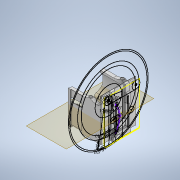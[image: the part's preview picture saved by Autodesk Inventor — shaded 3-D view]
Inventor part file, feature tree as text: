
AUTODESK INVENTOR PART (.ipt)
format: ipt  version: 2022 (Build 260153000, 153)  size: 979,968 bytes
history: native  units: mm
features: sketch x25, reference x24, extrude x23, projected_geometry x19, fillet x15, other x12, chamfer x2
ambient origin geometry x8: Origin, YZ Plane, XZ Plane, XY Plane, X Axis, Y Axis, Z Axis, Center Point
bodies: Body1 (feature_tree)
feature tree (120):
  other  "Твердое тело1"
  extrude  "Выдавливание1"  Depth=34.5mm TaperAngle=0.0deg
  extrude  "Выдавливание2"  Depth=0.5mm
  extrude  "Выдавливание3"  Depth=0.3mm
  extrude  "Выдавливание4"  Depth=5.0mm
  extrude  "Выдавливание5"  Depth=5.0mm
  extrude  "Выдавливание6"  Depth=5.0mm
  extrude  "Выдавливание8"  Depth=15.0mm
  extrude  "Выдавливание9"  Depth=15.0mm
  chamfer  "Фаска1"  Distance=15.0mm
  fillet  "Сопряжение1"  Radius=1.7mm
  extrude  "Выдавливание10"  Depth=2.0mm TaperAngle=0.0deg
  extrude  "Выдавливание11"  Depth=0.8mm
  fillet  "Сопряжение2"  Radius=4.7mm
  fillet  "Сопряжение3"  Radius=0.4mm
  fillet  "Сопряжение4"  Radius=0.4mm
  fillet  "Сопряжение5"  Radius=200.0mm
  sketch  "Эскиз15"
  extrude  "Выдавливание12"  Depth=0.5mm TaperAngle=0.0deg
  sketch  "Эскиз17"
  extrude  "Выдавливание13"  Depth=2.3mm TaperAngle=0.0deg
  extrude  "Выдавливание18"  Depth=10.0mm
  extrude  "Выдавливание19"  Depth=10.0mm
  extrude  "Выдавливание20"  Depth=3.0mm
  chamfer  "Фаска2"  Distance=4.0mm
  other  "РабПлоскость1"
  extrude  "Выдавливание21"  Depth=3.0mm
  fillet  "Сопряжение16"  Radius=4.0mm
  fillet  "Сопряжение17"  Radius=2.3mm
  fillet  "Сопряжение18"  Radius=2.3mm
  extrude  "Выдавливание22"  Depth=10.0mm
  fillet  "Сопряжение19"  Radius=45.0mm
  extrude  "Выдавливание23"  Depth=30.0mm
  extrude  "Выдавливание24"  Depth=0.8mm TaperAngle=0.0deg
  fillet  "Сопряжение20"  Radius=2.0mm
  extrude  "Выдавливание25"  Depth=1.5mm
  fillet  "Сопряжение21"  Radius=0.15mm
  extrude  "Выдавливание26"  Depth=3.0mm
  fillet  "Сопряжение22"  Radius=50.0mm
  fillet  "Сопряжение23"  Radius=4.0mm
  fillet  "Сопряжение24"  Radius=4.0mm
  extrude  "Выдавливание27"  Depth=3.2mm
  extrude  "Выдавливание28"  Depth=8.0mm
  fillet  "Сопряжение25"  Radius=2.2mm
  sketch  "Эскиз1"
  reference  "Ссылка1"
  reference  "Ссылка2"
  reference  "Ссылка3"
  reference  "Ссылка4"
  reference  "Ссылка5"
  reference  "Ссылка6"
  reference  "Ссылка7"
  reference  "Ссылка8"
  sketch  "Эскиз2"
  projected_geometry  "Спроецированная петля1"
  projected_geometry  "Спроецированная петля2"
  sketch  "Эскиз3"
  reference  "Ссылка9"
  reference  "Ссылка10"
  sketch  "Эскиз4"
  projected_geometry  "Спроецированная петля3"
  reference  "Ссылка11"
  reference  "Ссылка12"
  reference  "Ссылка13"
  reference  "Ссылка14"
  sketch  "Эскиз5"
  reference  "Ссылка15"
  reference  "Ссылка16"
  projected_geometry  "Спроецированная петля4"
  sketch  "Эскиз7"
  projected_geometry  "Спроецированная петля6"
  sketch  "Эскиз11"
  projected_geometry  "Спроецированная петля8"
  sketch  "Эскиз12"
  reference  "Ссылка27"
  sketch  "Эскиз13"
  reference  "Ссылка28"
  projected_geometry  "Спроецированная петля9"
  sketch  "Эскиз14"
  sketch  "Эскиз16"
  reference  "Ссылка29"
  projected_geometry  "Спроецированная петля10"
  projected_geometry  "Спроецированная петля11"
  projected_geometry  "Спроецированная петля12"
  reference  "Ссылка30"
  reference  "Ссылка31"
  sketch  "Эскиз18"
  projected_geometry  "Спроецированная петля14"
  sketch  "Эскиз23"
  sketch  "Эскиз24"
  projected_geometry  "Спроецированная петля24"
  sketch  "Эскиз25"
  sketch  "Эскиз26"
  sketch  "Эскиз27"
  projected_geometry  "Спроецированная петля25"
  sketch  "Эскиз28"
  sketch  "Эскиз29"
  projected_geometry  "Спроецированная петля26"
  sketch  "Эскиз30"
  projected_geometry  "Спроецированная петля27"
  projected_geometry  "Спроецированная петля28"
  projected_geometry  "Спроецированная петля29"
  reference  "Ссылка32"
  reference  "Ссылка33"
  sketch  "Эскиз31"
  reference  "Ссылка34"
  sketch  "Эскиз32"
  sketch  "Эскиз33"
  projected_geometry  "Спроецированная петля30"
  projected_geometry  "Спроецированная петля31"
  other  "<userpath>\OneDrive\Документы\Git\MZCAT_battery\FastBattery.iam"
  other  "FastBattery.iam"
  other  "plan:1"
  other  "BMS_board:1"
  other  "metal_body:1"
  other  "ButerBoard:1"
  other  "metal_cap:1"
  other  "<userpath>\Documents\Git\MZCAT_2024_construction\MZCAT_battery\FastBattery2.iam"
  other  "FastBattery2.iam"
  other  "metal_body_fixed:1"
